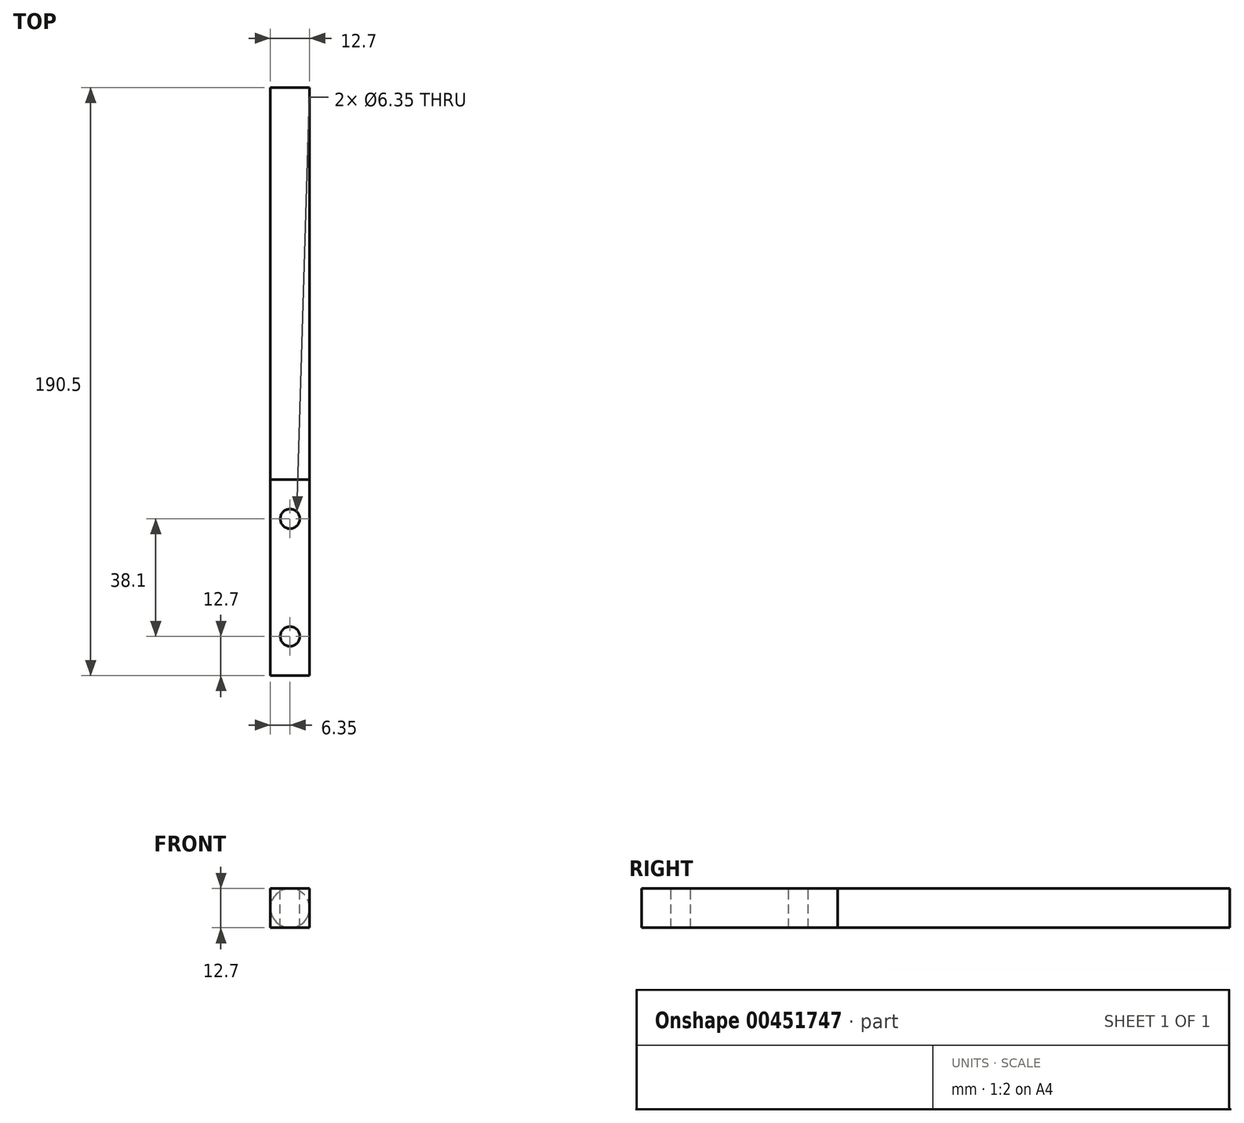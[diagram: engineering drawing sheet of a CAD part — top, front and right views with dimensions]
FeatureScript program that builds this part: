
annotation { "Feature Type Name" : "Feature", "Feature Type Description" : "" }
export const myFeature = defineFeature(function(context is Context, id is Id, definition is map)
    precondition{}
    {
        {
            var Q0;
            Q0=qCreatedBy(makeId("Front.planeOp"),FACE);
            var sketch = newSketch(context, id + "F0", { "sketchPlane" : qUnion([Q0])});
            skLineSegment(sketch, "E0.bottom", {"start": v(-6.35, 6.35) * mm, "end": v(6.35, 6.35) * mm});
            skLineSegment(sketch, "E0.top", {"start": v(-6.35, -6.35) * mm, "end": v(6.35, -6.35) * mm});
            skLineSegment(sketch, "E0.left", {"start": v(-6.35, 6.35) * mm, "end": v(-6.35, -6.35) * mm});
            skLineSegment(sketch, "E0.right", {"start": v(6.35, 6.35) * mm, "end": v(6.35, -6.35) * mm});
            skSolve(sketch);
        }
        {
            var Q0;
            Q0 = qSketchRegion(id + "F0", true);
            extrude(context, id + "F1", {"entities" : qUnion([Q0]), "depth" : 63.5 * mm});
        }
        {
            var Q0;
            Q0=makeQuery(id+"F1.opExtrude","SWEPT_FACE",FACE,{"disambiguationData":[OSD([sQuery(id+"F0.wireOp",EDGE,"E0.bottom")])]});
            var sketch = newSketch(context, id + "F2", { "sketchPlane" : qUnion([Q0])});
            skCircle(sketch, "E1", {"center": v(0, -12.7) * mm, "radius": 3.18 * mm});
            skCircle(sketch, "E2", {"center": v(0, -50.8) * mm, "radius": 3.18 * mm});
            skSolve(sketch);
        }
        {
            var Q0;
            Q0 = qSketchRegion(id + "F2", true);
            extrude(context, id + "F3", {"entities" : qUnion([Q0]), "operationType" : NewBodyOperationType.REMOVE, "oppositeDirection" : true, "depth" : 25.4 * mm});
        }
        {
            var Q0;
            Q0=makeQuery(id+"F1.opExtrude","CAP_FACE",FACE,{"disambiguationData":[OSD([sQuery(id+"F0.wireOp",EDGE,"E0.bottom"),sQuery(id+"F0.wireOp",EDGE,"E0.top"),sQuery(id+"F0.wireOp",EDGE,"E0.left"),sQuery(id+"F0.wireOp",EDGE,"E0.right")])],"isStart":true});
            var sketch = newSketch(context, id + "F4", { "sketchPlane" : qUnion([Q0])});
            skCircle(sketch, "E3", {"center": v(0, 0) * mm, "radius": 6.35 * mm});
            skSolve(sketch);
        }
        {
            var Q0;
            Q0 = qSketchRegion(id + "F4", true);
            extrude(context, id + "F5", {"entities" : qUnion([Q0]), "operationType" : NewBodyOperationType.ADD, "depth" : 127 * mm});
        }
    });
